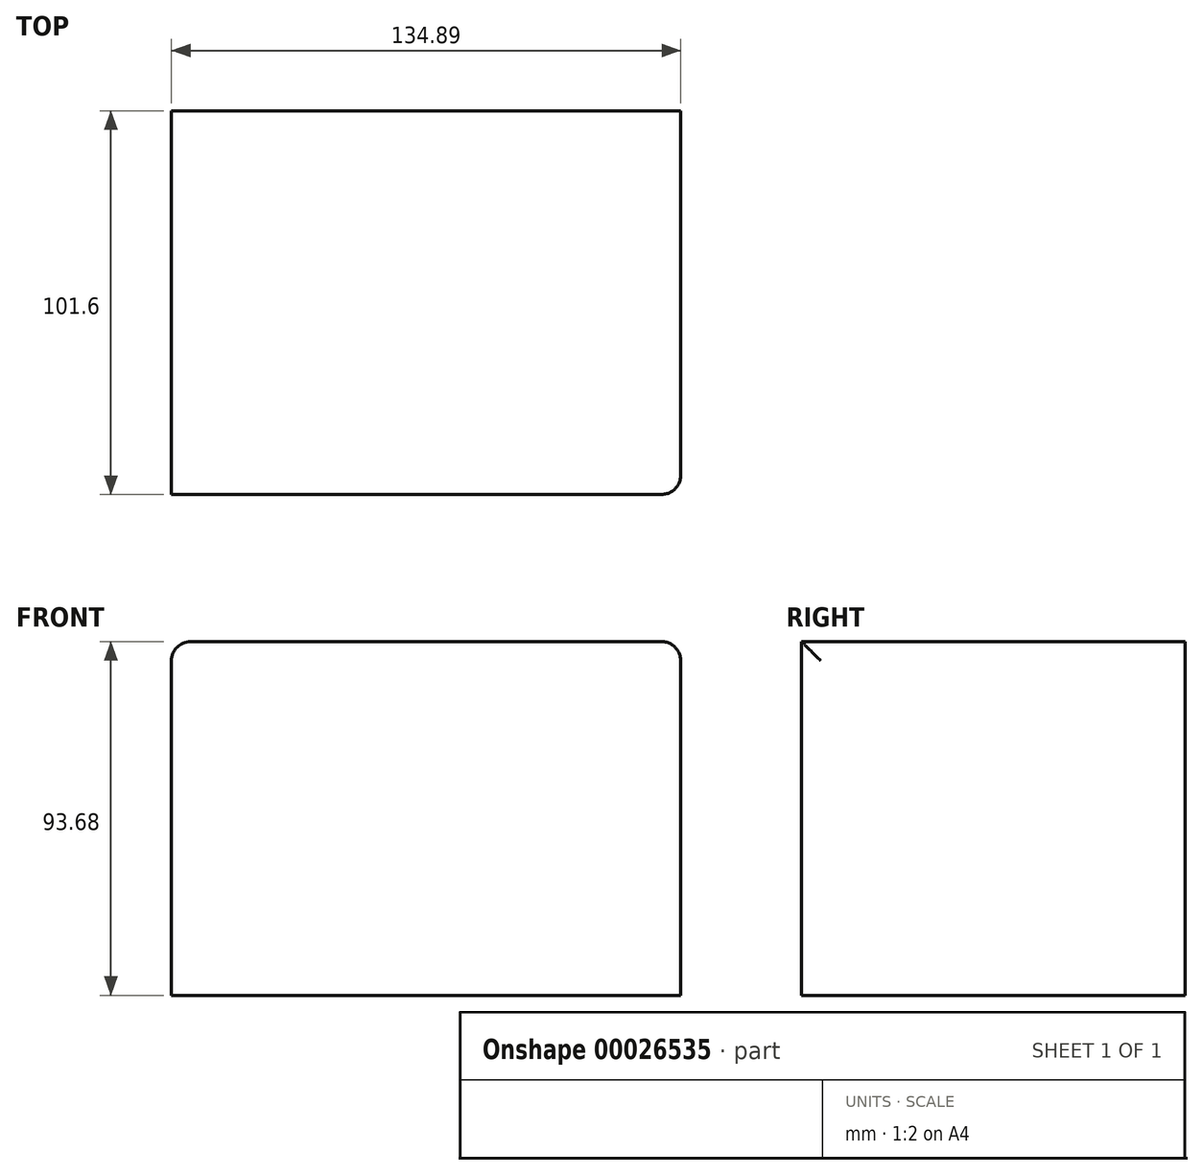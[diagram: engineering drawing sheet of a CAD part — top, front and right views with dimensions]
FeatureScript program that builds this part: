
annotation { "Feature Type Name" : "Feature", "Feature Type Description" : "" }
export const myFeature = defineFeature(function(context is Context, id is Id, definition is map)
    precondition{}
    {
        {
            var Q0;
            Q0=qCreatedBy(makeId("Front.planeOp"),FACE);
            var sketch = newSketch(context, id + "F0", { "sketchPlane" : qUnion([Q0])});
            skLineSegment(sketch, "E0.bottom", {"start": v(-65.94, 51.47) * mm, "end": v(68.95, 51.47) * mm});
            skLineSegment(sketch, "E0.top", {"start": v(-65.94, -42.21) * mm, "end": v(68.95, -42.21) * mm});
            skLineSegment(sketch, "E0.left", {"start": v(-65.94, 51.47) * mm, "end": v(-65.94, -42.21) * mm});
            skLineSegment(sketch, "E0.right", {"start": v(68.95, 51.47) * mm, "end": v(68.95, -42.21) * mm});
            skSolve(sketch);
        }
        {
            var Q0;
            Q0=makeQuery(id+"F0.imprint","IMPRINT",FACE,{"disambiguationData":[TD([[makeQuery(id+"F0.imprint","IMPRINT",EDGE,{"derivedFrom":sQuery(id+"F0.wireOp",EDGE,"E0.bottom")}),-1.0]])]});
            extrude(context, id + "F1", {"entities" : qUnion([Q0]), "depth" : 101.6 * mm});
        }
        {
            var Q0;
            Q0=makeQuery(id+"F1.opExtrude","SWEPT_EDGE",EDGE,{"disambiguationData":[OSD([sQuery(id+"F0.wireOp",EDGE,"E0.bottom"),sQuery(id+"F0.wireOp",EDGE,"E0.left")])]});
            var Q1;
            Q1=makeQuery(id+"F1.opExtrude","SWEPT_EDGE",EDGE,{"disambiguationData":[OSD([sQuery(id+"F0.wireOp",EDGE,"E0.bottom"),sQuery(id+"F0.wireOp",EDGE,"E0.right")])]});
            var Q2;
            Q2=makeQuery(id+"F1.opExtrude","CAP_EDGE",EDGE,{"disambiguationData":[OSD([sQuery(id+"F0.wireOp",EDGE,"E0.right")])],"isStart":false});
            fillet(context, id + "F2", {"entities" : qUnion([Q0, Q1, Q2]), "radius" : 5.08 * mm, "tangentPropagation" : true, "allowEdgeOverflow" : false});
        }
    });
